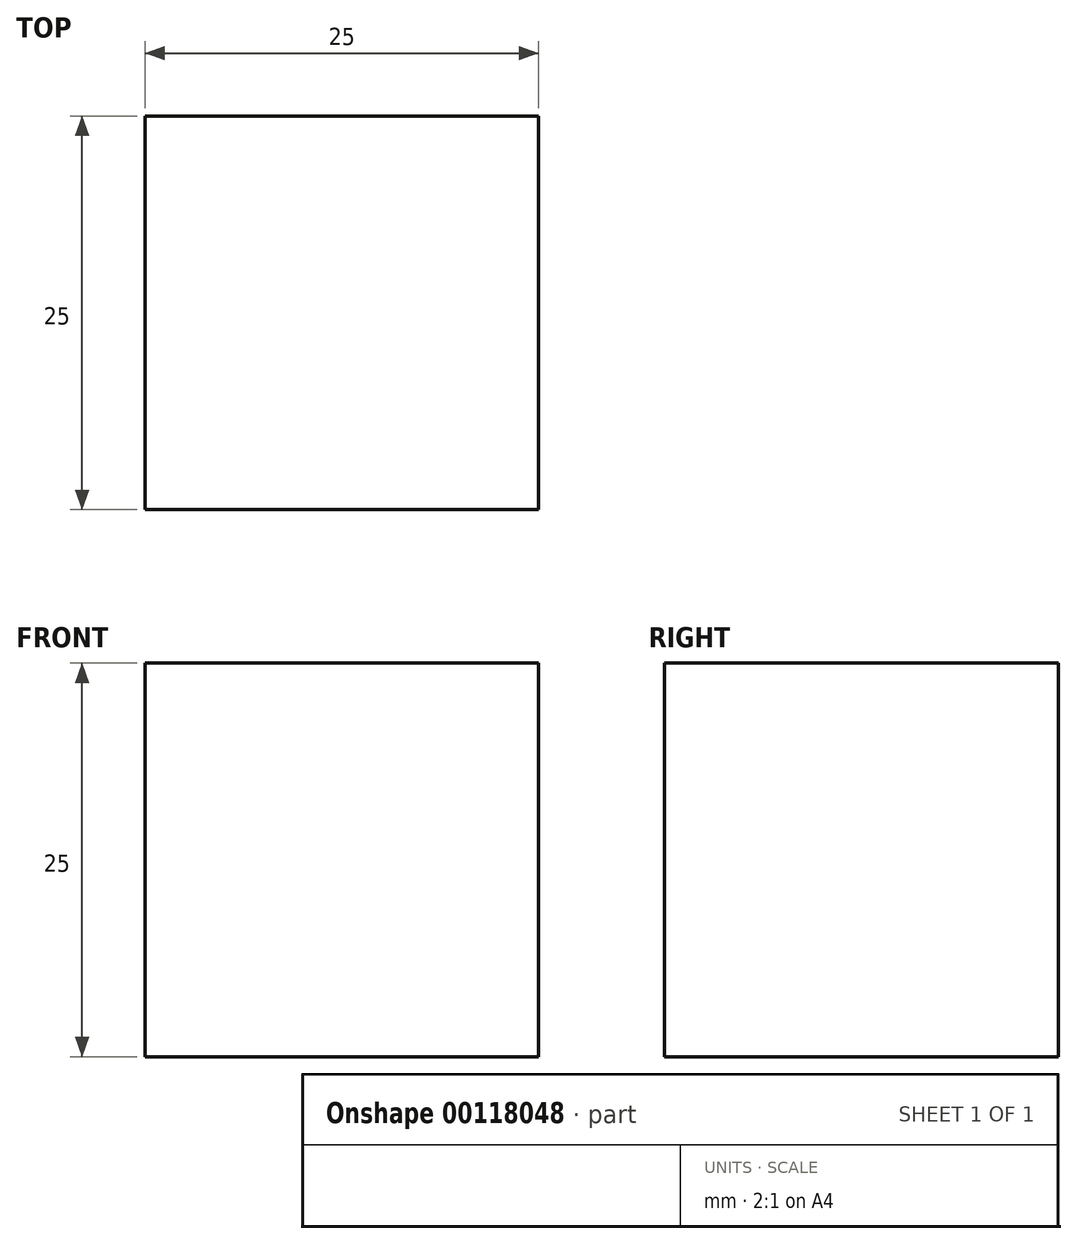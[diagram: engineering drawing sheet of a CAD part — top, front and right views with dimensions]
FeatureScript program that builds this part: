
annotation { "Feature Type Name" : "Feature", "Feature Type Description" : "" }
export const myFeature = defineFeature(function(context is Context, id is Id, definition is map)
    precondition{}
    {
        {
            var Q0;
            Q0=qCreatedBy(makeId("Front.planeOp"),FACE);
            var sketch = newSketch(context, id + "F0", { "sketchPlane" : qUnion([Q0])});
            skLineSegment(sketch, "E0.bottom", {"start": v(0, 0) * mm, "end": v(25, 0) * mm});
            skLineSegment(sketch, "E0.top", {"start": v(0, 25) * mm, "end": v(25, 25) * mm});
            skLineSegment(sketch, "E0.left", {"start": v(0, 0) * mm, "end": v(0, 25) * mm});
            skLineSegment(sketch, "E0.right", {"start": v(25, 0) * mm, "end": v(25, 25) * mm});
            skSolve(sketch);
        }
        {
            var Q0;
            Q0=makeQuery(id+"F0.imprint","IMPRINT",FACE,{"disambiguationData":[TD([[makeQuery(id+"F0.imprint","IMPRINT",EDGE,{"derivedFrom":sQuery(id+"F0.wireOp",EDGE,"E0.bottom")}),1.0]])]});
            var Q1;
            Q1 = qSketchRegion(id + "F0", true);
            extrude(context, id + "F1", {"entities" : qUnion([Q0, Q1]), "depth" : 25 * mm});
        }
    });
